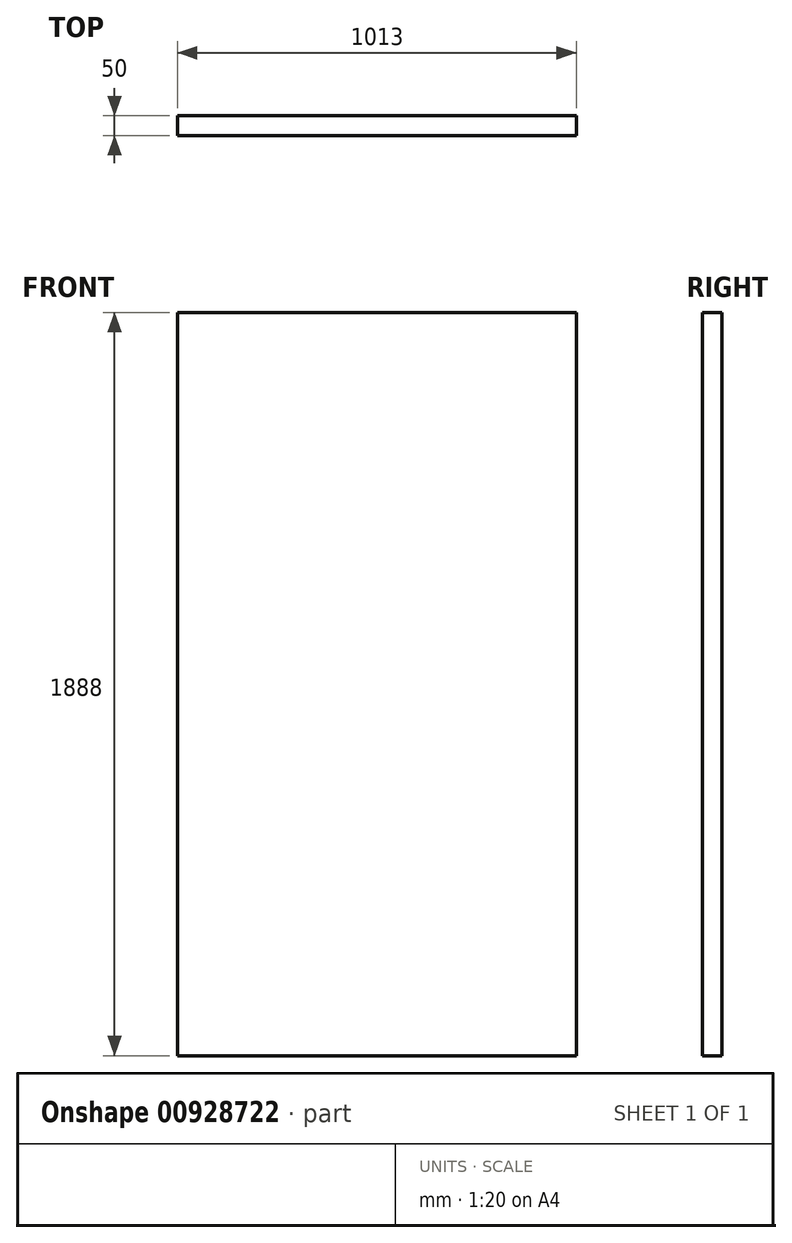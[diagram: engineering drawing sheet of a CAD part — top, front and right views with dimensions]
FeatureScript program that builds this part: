
annotation { "Feature Type Name" : "Feature", "Feature Type Description" : "" }
export const myFeature = defineFeature(function(context is Context, id is Id, definition is map)
    precondition{}
    {
        {
            var Q0;
            Q0=qCreatedBy(makeId("Front.planeOp"),FACE);
            var sketch = newSketch(context, id + "F0", { "sketchPlane" : qUnion([Q0])});
            skLineSegment(sketch, "E0.bottom", {"start": v(506.5, 944) * mm, "end": v(-506.5, 944) * mm});
            skLineSegment(sketch, "E0.top", {"start": v(506.5, -944) * mm, "end": v(-506.5, -944) * mm});
            skLineSegment(sketch, "E0.left", {"start": v(506.5, 944) * mm, "end": v(506.5, -944) * mm});
            skLineSegment(sketch, "E0.right", {"start": v(-506.5, 944) * mm, "end": v(-506.5, -944) * mm});
            skPoint(sketch, "E0.middle", {"position": v(0, 0) * mm});
            skSolve(sketch);
        }
        {
            var Q0;
            Q0=makeQuery(id+"F0.imprint","IMPRINT",FACE,{"disambiguationData":[TD([[makeQuery(id+"F0.imprint","IMPRINT",EDGE,{"derivedFrom":sQuery(id+"F0.wireOp",EDGE,"E0.bottom")}),1.0]])]});
            extrude(context, id + "F1", {"entities" : qUnion([Q0]), "depth" : 50 * mm, "offsetDistance" : 25 * mm});
        }
    });
